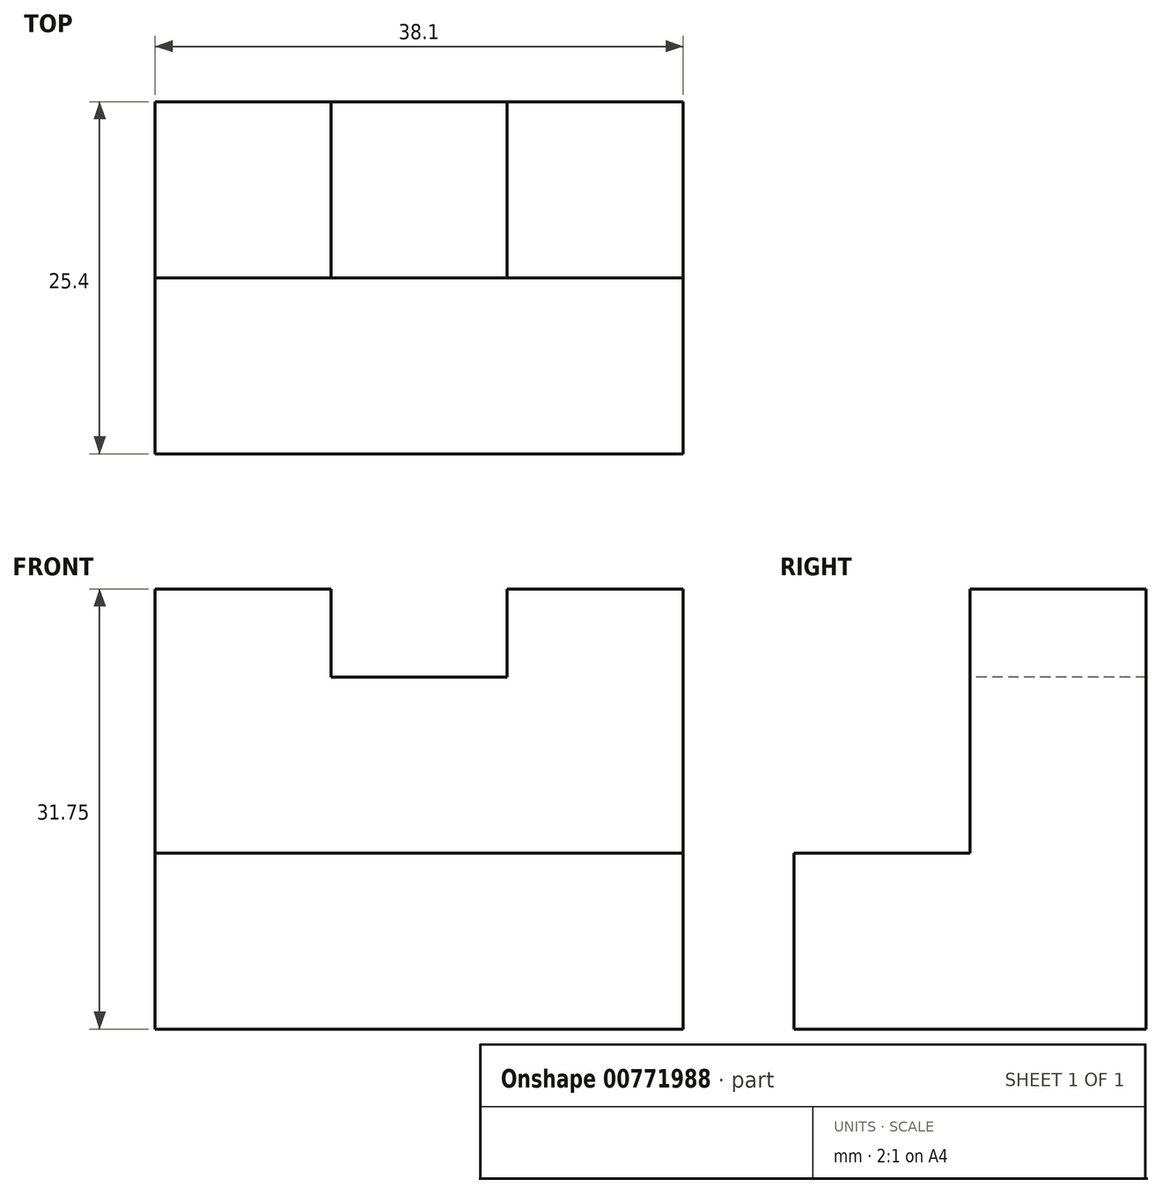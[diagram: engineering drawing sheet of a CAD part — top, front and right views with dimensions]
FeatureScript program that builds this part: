
annotation { "Feature Type Name" : "Feature", "Feature Type Description" : "" }
export const myFeature = defineFeature(function(context is Context, id is Id, definition is map)
    precondition{}
    {
        {
            var Q0;
            Q0=qCreatedBy(makeId("Front.planeOp"),FACE);
            var sketch = newSketch(context, id + "F0", { "sketchPlane" : qUnion([Q0])});
            skLineSegment(sketch, "E0", {"start": v(0, 0) * mm, "end": v(38.1, 0) * mm});
            skLineSegment(sketch, "E1", {"start": v(0, 0) * mm, "end": v(0, 31.75) * mm});
            skLineSegment(sketch, "E2", {"start": v(0, 31.75) * mm, "end": v(38.1, 31.75) * mm});
            skLineSegment(sketch, "E3", {"start": v(38.1, 31.75) * mm, "end": v(38.1, 0) * mm});
            skSolve(sketch);
        }
        {
            var Q0;
            Q0 = qSketchRegion(id + "F0", true);
            extrude(context, id + "F1", {"entities" : qUnion([Q0]), "depth" : 25.4 * mm, "offsetDistance" : 25.4 * mm});
        }
        {
            var Q0;
            Q0=makeQuery(id+"F1.opExtrude","CAP_FACE",FACE,{"disambiguationData":[OSD([sQuery(id+"F0.wireOp",EDGE,"E0"),sQuery(id+"F0.wireOp",EDGE,"E1"),sQuery(id+"F0.wireOp",EDGE,"E2"),sQuery(id+"F0.wireOp",EDGE,"E3")])],"isStart":false});
            var sketch = newSketch(context, id + "F2", { "sketchPlane" : qUnion([Q0])});
            skLineSegment(sketch, "E4", {"start": v(38.1, 0) * mm, "end": v(38.1, 12.7) * mm});
            skLineSegment(sketch, "E5", {"start": v(0, 0) * mm, "end": v(0, 12.7) * mm});
            skLineSegment(sketch, "E6", {"start": v(38.1, 12.7) * mm, "end": v(0, 12.7) * mm});
            skSolve(sketch);
        }
        {
            var Q0;
            {var subQ0=sQuery(id+"F2.wireOp",EDGE,"E6");Q0=makeQuery(id+"F2.imprint","IMPRINT",FACE,{"disambiguationData":[TD([[makeQuery(id+"F2.imprint","IMPRINT",EDGE,{"derivedFrom":subQ0}),-1.0]])]});}
            extrude(context, id + "F3", {"entities" : qUnion([Q0]), "operationType" : NewBodyOperationType.REMOVE, "oppositeDirection" : true, "depth" : 12.7 * mm, "offsetDistance" : 25.4 * mm});
        }
        {
            var Q0;
            Q0=makeQuery(id+"F3.boolean.opBoolean","COPY",FACE,{"derivedFrom":makeQuery(id+"F3.opExtrude","CAP_FACE",FACE,{"disambiguationData":[OSD([sQuery(id+"F0.wireOp",EDGE,"E1"),sQuery(id+"F0.wireOp",EDGE,"E2"),sQuery(id+"F0.wireOp",EDGE,"E3"),sQuery(id+"F2.wireOp",EDGE,"E6")])],"isStart":false})});
            var sketch = newSketch(context, id + "F4", { "sketchPlane" : qUnion([Q0])});
            skLineSegment(sketch, "E7", {"start": v(0, 31.75) * mm, "end": v(12.7, 31.75) * mm});
            skLineSegment(sketch, "E8", {"start": v(38.1, 31.75) * mm, "end": v(25.4, 31.75) * mm});
            skLineSegment(sketch, "E9", {"start": v(25.4, 31.75) * mm, "end": v(25.4, 25.4) * mm});
            skLineSegment(sketch, "E10", {"start": v(12.7, 31.75) * mm, "end": v(12.7, 25.4) * mm});
            skLineSegment(sketch, "E11", {"start": v(12.7, 25.4) * mm, "end": v(25.4, 25.4) * mm});
            skSolve(sketch);
        }
        {
            var Q0;
            {var subQ0=sQuery(id+"F4.wireOp",EDGE,"E9");Q0=makeQuery(id+"F4.imprint","IMPRINT",FACE,{"disambiguationData":[TD([[makeQuery(id+"F4.imprint","IMPRINT",EDGE,{"derivedFrom":subQ0}),-1.0]])]});}
            extrude(context, id + "F5", {"entities" : qUnion([Q0]), "operationType" : NewBodyOperationType.REMOVE, "oppositeDirection" : true, "depth" : 25.4 * mm, "offsetDistance" : 25.4 * mm});
        }
    });
